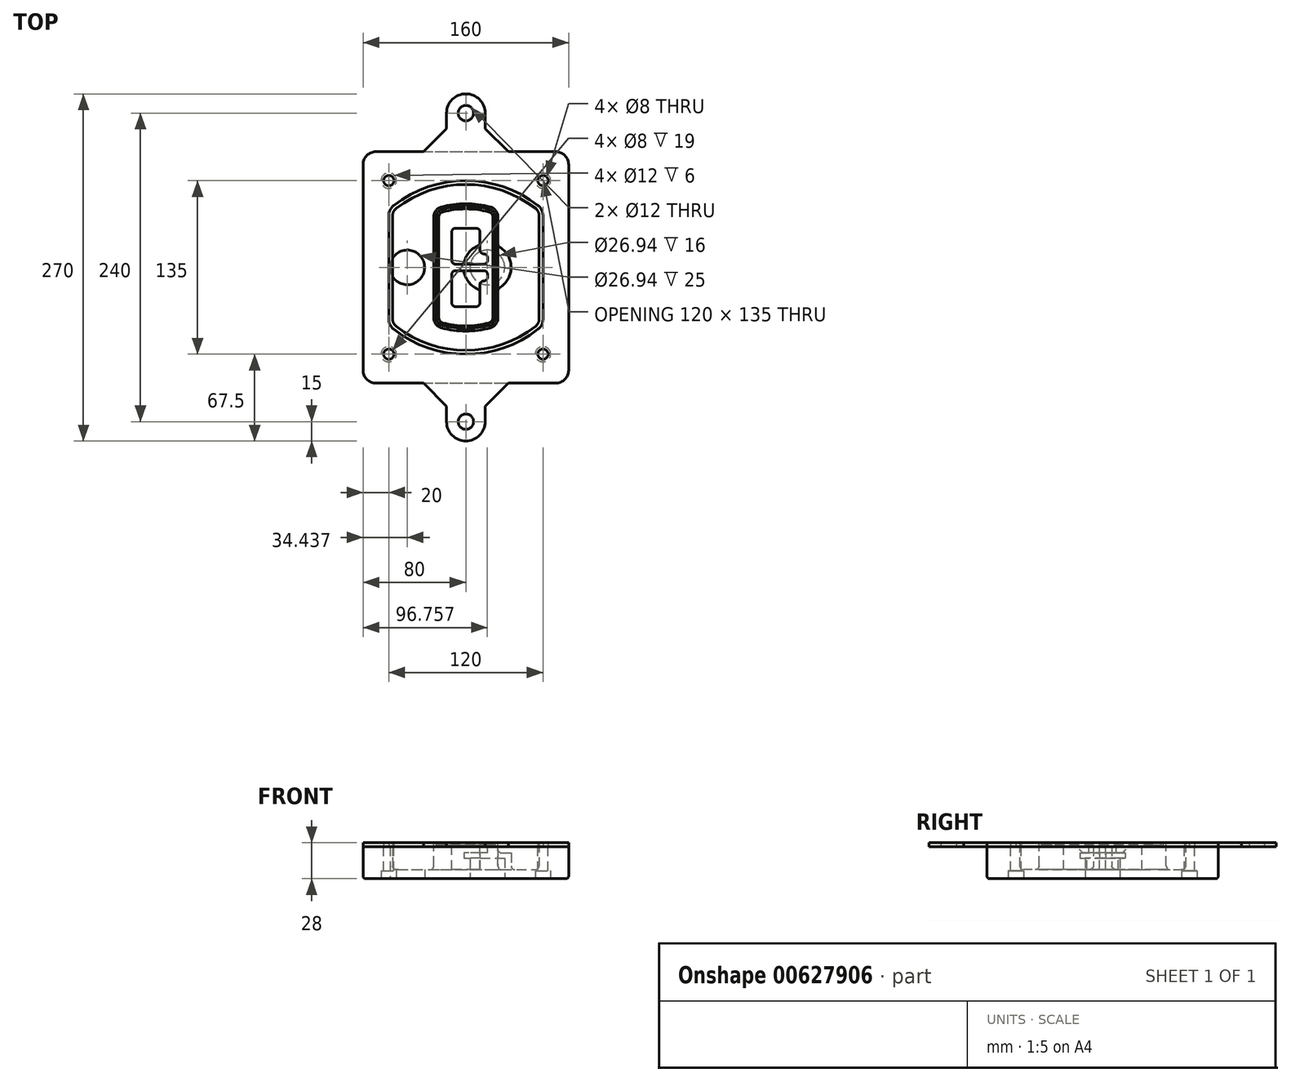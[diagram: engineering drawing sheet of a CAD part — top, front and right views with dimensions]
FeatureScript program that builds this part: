
annotation { "Feature Type Name" : "Feature", "Feature Type Description" : "" }
export const myFeature = defineFeature(function(context is Context, id is Id, definition is map)
    precondition{}
    {
        {
            var Q0;
            Q0=qCreatedBy(makeId("Top.planeOp"),FACE);
            var sketch = newSketch(context, id + "F0", { "sketchPlane" : qUnion([Q0])});
            skPoint(sketch, "E0.rect.middle", {"position": v(0, 0) * mm});
            skLineSegment(sketch, "E1.bottom", {"start": v(-70, -90) * mm, "end": v(70, -90) * mm});
            skLineSegment(sketch, "E1.top", {"start": v(-70, 90) * mm, "end": v(70, 90) * mm});
            skLineSegment(sketch, "E1.left", {"start": v(-80, -80) * mm, "end": v(-80, 80) * mm});
            skLineSegment(sketch, "E1.right", {"start": v(80, -80) * mm, "end": v(80, 80) * mm});
            skLineSegment(sketch, "E2", {"start": v(-80, 90) * mm, "end": v(80, -90) * mm, "construction": true});
            skLineSegment(sketch, "E3", {"start": v(80, 90) * mm, "end": v(-80, -90) * mm, "construction": true});
            skCircle(sketch, "E4", {"center": v(-60, 67.5) * mm, "radius": 4 * mm});
            skCircle(sketch, "E5", {"center": v(60, 67.5) * mm, "radius": 4 * mm});
            skCircle(sketch, "E6", {"center": v(60, -67.5) * mm, "radius": 4 * mm});
            skCircle(sketch, "E7", {"center": v(-60, -67.5) * mm, "radius": 4 * mm});
            skLineSegment(sketch, "E8", {"start": v(-60, 67.5) * mm, "end": v(60, 67.5) * mm, "construction": true});
            skLineSegment(sketch, "E9", {"start": v(60, 67.5) * mm, "end": v(60, -67.5) * mm, "construction": true});
            skLineSegment(sketch, "E10", {"start": v(60, -67.5) * mm, "end": v(-60, -67.5) * mm, "construction": true});
            skLineSegment(sketch, "E11", {"start": v(-60, -67.5) * mm, "end": v(-60, 67.5) * mm, "construction": true});
            skLineSegment(sketch, "E12", {"start": v(-60, 40.3) * mm, "end": v(-60, -40.3) * mm});
            skLineSegment(sketch, "E13", {"start": v(60, 40.3) * mm, "end": v(60, -40.3) * mm});
            skArc(sketch, "E14", {"start": v(56.15, 48.18) * mm, "mid": v(0, 67.5) * mm, "end": v(-56.15, 48.18) * mm});
            skArc(sketch, "E15", {"start": v(-56.15, -48.18) * mm, "mid": v(0, -67.5) * mm, "end": v(56.15, -48.18) * mm});
            skLineSegment(sketch, "E16", {"start": v(-60, 0) * mm, "end": v(60, 0) * mm, "construction": true});
            skPoint(sketch, "E17.visualSharp", {"position": v(-60, -45) * mm});
            skArc(sketch, "E17.filletArc", {"start": v(-60, -40.3) * mm, "mid": v(-58.99, -44.68) * mm, "end": v(-56.15, -48.18) * mm});
            skPoint(sketch, "E18.visualSharp", {"position": v(-60, 45) * mm});
            skArc(sketch, "E18.filletArc", {"start": v(-56.15, 48.18) * mm, "mid": v(-58.99, 44.68) * mm, "end": v(-60, 40.3) * mm});
            skPoint(sketch, "E19.visualSharp", {"position": v(60, 45) * mm});
            skArc(sketch, "E19.filletArc", {"start": v(60, 40.3) * mm, "mid": v(58.99, 44.68) * mm, "end": v(56.15, 48.18) * mm});
            skPoint(sketch, "E20.visualSharp", {"position": v(60, -45) * mm});
            skArc(sketch, "E20.filletArc", {"start": v(56.15, -48.18) * mm, "mid": v(58.99, -44.68) * mm, "end": v(60, -40.3) * mm});
            skPoint(sketch, "E21.visualSharp", {"position": v(-80, 90) * mm});
            skArc(sketch, "E21.filletArc", {"start": v(-70, 90) * mm, "mid": v(-77.07, 87.07) * mm, "end": v(-80, 80) * mm});
            skPoint(sketch, "E22.visualSharp", {"position": v(80, 90) * mm});
            skArc(sketch, "E22.filletArc", {"start": v(80, 80) * mm, "mid": v(77.07, 87.07) * mm, "end": v(70, 90) * mm});
            skPoint(sketch, "E23.visualSharp", {"position": v(80, -90) * mm});
            skArc(sketch, "E23.filletArc", {"start": v(70, -90) * mm, "mid": v(77.07, -87.07) * mm, "end": v(80, -80) * mm});
            skPoint(sketch, "E24.visualSharp", {"position": v(-80, -90) * mm});
            skArc(sketch, "E24.filletArc", {"start": v(-80, -80) * mm, "mid": v(-77.07, -87.07) * mm, "end": v(-70, -90) * mm});
            skArc(sketch, "E25.0", {"start": v(57, 40.3) * mm, "mid": v(56.3, 43.36) * mm, "end": v(54.3, 45.81) * mm});
            skLineSegment(sketch, "E25.1", {"start": v(57, 40.3) * mm, "end": v(57, -40.3) * mm});
            skArc(sketch, "E25.2", {"start": v(54.3, -45.81) * mm, "mid": v(56.3, -43.36) * mm, "end": v(57, -40.3) * mm});
            skArc(sketch, "E25.3", {"start": v(-54.3, -45.81) * mm, "mid": v(0, -64.5) * mm, "end": v(54.3, -45.81) * mm});
            skArc(sketch, "E25.4", {"start": v(-57, -40.3) * mm, "mid": v(-56.3, -43.36) * mm, "end": v(-54.3, -45.81) * mm});
            skArc(sketch, "E25.5", {"start": v(54.3, 45.81) * mm, "mid": v(0, 64.5) * mm, "end": v(-54.3, 45.81) * mm});
            skLineSegment(sketch, "E25.6", {"start": v(-57, 40.3) * mm, "end": v(-57, -40.3) * mm});
            skArc(sketch, "E25.7", {"start": v(-54.3, 45.81) * mm, "mid": v(-56.3, 43.36) * mm, "end": v(-57, 40.3) * mm});
            skArc(sketch, "E26.0", {"start": v(-58.62, 51.33) * mm, "mid": v(-62.58, 46.43) * mm, "end": v(-64, 40.3) * mm});
            skArc(sketch, "E26.1", {"start": v(58.62, 51.33) * mm, "mid": v(0, 71.5) * mm, "end": v(-58.62, 51.33) * mm});
            skArc(sketch, "E26.2", {"start": v(64, 40.3) * mm, "mid": v(62.58, 46.43) * mm, "end": v(58.62, 51.33) * mm});
            skLineSegment(sketch, "E26.3", {"start": v(64, 40.3) * mm, "end": v(64, -40.3) * mm});
            skArc(sketch, "E26.4", {"start": v(58.62, -51.33) * mm, "mid": v(62.58, -46.43) * mm, "end": v(64, -40.3) * mm});
            skLineSegment(sketch, "E26.5", {"start": v(-64, 40.3) * mm, "end": v(-64, -40.3) * mm});
            skArc(sketch, "E26.6", {"start": v(-58.62, -51.33) * mm, "mid": v(0, -71.5) * mm, "end": v(58.62, -51.33) * mm});
            skArc(sketch, "E26.7", {"start": v(-64, -40.3) * mm, "mid": v(-62.58, -46.43) * mm, "end": v(-58.62, -51.33) * mm});
            skSolve(sketch);
        }
        {
            var Q0;
            Q0=makeQuery(id+"F0.imprint","IMPRINT",FACE,{"disambiguationData":[TD([[makeQuery(id+"F0.imprint","IMPRINT",EDGE,{"derivedFrom":sQuery(id+"F0.wireOp",EDGE,"E1.bottom")}),1.0]])]});
            var Q1;
            Q1=makeQuery(id+"F0.imprint","IMPRINT",FACE,{"disambiguationData":[TD([[makeQuery(id+"F0.imprint","IMPRINT",EDGE,{"derivedFrom":sQuery(id+"F0.wireOp",EDGE,"E12")}),1.0]])]});
            var Q2;
            Q2=makeQuery(id+"F0.imprint","IMPRINT",FACE,{"disambiguationData":[TD([[makeQuery(id+"F0.imprint","IMPRINT",EDGE,{"derivedFrom":sQuery(id+"F0.wireOp",EDGE,"E25.0")}),1.0]])]});
            var Q3;
            Q3=makeQuery(id+"F0.imprint","IMPRINT",FACE,{"disambiguationData":[TD([[makeQuery(id+"F0.imprint","IMPRINT",EDGE,{"derivedFrom":sQuery(id+"F0.wireOp",EDGE,"E12")}),-1.0]])]});
            extrude(context, id + "F1", {"entities" : qUnion([Q0, Q1, Q2, Q3]), "oppositeDirection" : true, "depth" : 25 * mm});
        }
        {
            var Q0;
            Q0=makeQuery(id+"F0.imprint","IMPRINT",FACE,{"disambiguationData":[TD([[makeQuery(id+"F0.imprint","IMPRINT",EDGE,{"derivedFrom":sQuery(id+"F0.wireOp",EDGE,"E12")}),1.0]])]});
            extrude(context, id + "F2", {"entities" : qUnion([Q0]), "operationType" : NewBodyOperationType.ADD, "depth" : 3 * mm});
        }
        {
            var Q0;
            Q0=makeQuery(id+"F0.imprint","IMPRINT",FACE,{"disambiguationData":[TD([[makeQuery(id+"F0.imprint","IMPRINT",EDGE,{"derivedFrom":sQuery(id+"F0.wireOp",EDGE,"E25.0")}),1.0]])]});
            extrude(context, id + "F3", {"entities" : qUnion([Q0]), "operationType" : NewBodyOperationType.REMOVE, "oppositeDirection" : true, "depth" : 18 * mm});
        }
        {
            var Q0;
            Q0=makeQuery(id+"F2.opExtrude","CAP_FACE",FACE,{"disambiguationData":[OSD([sQuery(id+"F0.wireOp",EDGE,"E12"),sQuery(id+"F0.wireOp",EDGE,"E13"),sQuery(id+"F0.wireOp",EDGE,"E14"),sQuery(id+"F0.wireOp",EDGE,"E15"),sQuery(id+"F0.wireOp",EDGE,"E17.filletArc"),sQuery(id+"F0.wireOp",EDGE,"E18.filletArc"),sQuery(id+"F0.wireOp",EDGE,"E19.filletArc"),sQuery(id+"F0.wireOp",EDGE,"E20.filletArc"),sQuery(id+"F0.wireOp",EDGE,"E25.0"),sQuery(id+"F0.wireOp",EDGE,"E25.1"),sQuery(id+"F0.wireOp",EDGE,"E25.2"),sQuery(id+"F0.wireOp",EDGE,"E25.3"),sQuery(id+"F0.wireOp",EDGE,"E25.4"),sQuery(id+"F0.wireOp",EDGE,"E25.5"),sQuery(id+"F0.wireOp",EDGE,"E25.6"),sQuery(id+"F0.wireOp",EDGE,"E25.7")])],"isStart":false});
            var sketch = newSketch(context, id + "F4", { "sketchPlane" : qUnion([Q0])});
            skArc(sketch, "E27.0", {"start": v(-19.08, -46.97) * mm, "mid": v(0, -49.5) * mm, "end": v(19.08, -46.97) * mm});
            skArc(sketch, "E28.0", {"start": v(19.08, 46.97) * mm, "mid": v(0, 49.5) * mm, "end": v(-19.08, 46.97) * mm});
            skLineSegment(sketch, "E29", {"start": v(-25, 39.25) * mm, "end": v(-25, -39.25) * mm});
            skLineSegment(sketch, "E30", {"start": v(25, 39.25) * mm, "end": v(25, -39.25) * mm});
            skLineSegment(sketch, "E31", {"start": v(-25, 45.1) * mm, "end": v(25, 45.1) * mm, "construction": true});
            skLineSegment(sketch, "E32", {"start": v(-25, -45.1) * mm, "end": v(25, -45.1) * mm, "construction": true});
            skPoint(sketch, "E33.visualSharp", {"position": v(-25, 45.1) * mm});
            skArc(sketch, "E33.filletArc", {"start": v(-19.08, 46.97) * mm, "mid": v(-23.35, 44.11) * mm, "end": v(-25, 39.25) * mm});
            skPoint(sketch, "E34.visualSharp", {"position": v(25, 45.1) * mm});
            skArc(sketch, "E34.filletArc", {"start": v(25, 39.25) * mm, "mid": v(23.35, 44.11) * mm, "end": v(19.08, 46.97) * mm});
            skPoint(sketch, "E35.visualSharp", {"position": v(25, -45.1) * mm});
            skArc(sketch, "E35.filletArc", {"start": v(19.08, -46.97) * mm, "mid": v(23.35, -44.11) * mm, "end": v(25, -39.25) * mm});
            skPoint(sketch, "E36.visualSharp", {"position": v(-25, -45.1) * mm});
            skArc(sketch, "E36.filletArc", {"start": v(-25, -39.25) * mm, "mid": v(-23.35, -44.11) * mm, "end": v(-19.08, -46.97) * mm});
            skArc(sketch, "E37.0", {"start": v(54.3, 45.81) * mm, "mid": v(0, 64.5) * mm, "end": v(-54.3, 45.81) * mm});
            skArc(sketch, "E37.1", {"start": v(-54.3, 45.81) * mm, "mid": v(-56.3, 43.36) * mm, "end": v(-57, 40.3) * mm});
            skLineSegment(sketch, "E37.2", {"start": v(-57, 40.3) * mm, "end": v(-57, -40.3) * mm});
            skArc(sketch, "E37.3", {"start": v(-57, -40.3) * mm, "mid": v(-56.3, -43.36) * mm, "end": v(-54.3, -45.81) * mm});
            skArc(sketch, "E37.4", {"start": v(-54.3, -45.81) * mm, "mid": v(0, -64.5) * mm, "end": v(54.3, -45.81) * mm});
            skArc(sketch, "E37.5", {"start": v(54.3, -45.81) * mm, "mid": v(56.3, -43.36) * mm, "end": v(57, -40.3) * mm});
            skLineSegment(sketch, "E37.6", {"start": v(57, 40.3) * mm, "end": v(57, -40.3) * mm});
            skArc(sketch, "E37.7", {"start": v(57, 40.3) * mm, "mid": v(56.3, 43.36) * mm, "end": v(54.3, 45.81) * mm});
            skLineSegment(sketch, "E38.0", {"start": v(23, 39.25) * mm, "end": v(23, -39.25) * mm});
            skArc(sketch, "E38.1", {"start": v(18.56, -45.04) * mm, "mid": v(21.76, -42.9) * mm, "end": v(23, -39.25) * mm});
            skArc(sketch, "E38.2", {"start": v(-18.56, -45.04) * mm, "mid": v(0, -47.5) * mm, "end": v(18.56, -45.04) * mm});
            skArc(sketch, "E38.3", {"start": v(-23, -39.25) * mm, "mid": v(-21.76, -42.9) * mm, "end": v(-18.56, -45.04) * mm});
            skLineSegment(sketch, "E38.4", {"start": v(-23, 39.25) * mm, "end": v(-23, -39.25) * mm});
            skArc(sketch, "E38.5", {"start": v(23, 39.25) * mm, "mid": v(21.76, 42.9) * mm, "end": v(18.56, 45.04) * mm});
            skArc(sketch, "E38.6", {"start": v(-18.56, 45.04) * mm, "mid": v(-21.76, 42.9) * mm, "end": v(-23, 39.25) * mm});
            skArc(sketch, "E38.7", {"start": v(18.56, 45.04) * mm, "mid": v(0, 47.5) * mm, "end": v(-18.56, 45.04) * mm});
            skArc(sketch, "E39.0", {"start": v(21, 39.25) * mm, "mid": v(20.18, 41.68) * mm, "end": v(18.04, 43.1) * mm});
            skLineSegment(sketch, "E39.1", {"start": v(21, 39.25) * mm, "end": v(21, -39.25) * mm});
            skArc(sketch, "E39.2", {"start": v(18.04, -43.1) * mm, "mid": v(20.18, -41.68) * mm, "end": v(21, -39.25) * mm});
            skArc(sketch, "E39.3", {"start": v(-18.04, -43.1) * mm, "mid": v(0, -45.5) * mm, "end": v(18.04, -43.1) * mm});
            skArc(sketch, "E39.4", {"start": v(-21, -39.25) * mm, "mid": v(-20.18, -41.68) * mm, "end": v(-18.04, -43.1) * mm});
            skArc(sketch, "E39.5", {"start": v(18.04, 43.1) * mm, "mid": v(0, 45.5) * mm, "end": v(-18.04, 43.1) * mm});
            skLineSegment(sketch, "E39.6", {"start": v(-21, 39.25) * mm, "end": v(-21, -39.25) * mm});
            skArc(sketch, "E39.7", {"start": v(-18.04, 43.1) * mm, "mid": v(-20.18, 41.68) * mm, "end": v(-21, 39.25) * mm});
            skLineSegment(sketch, "E40", {"start": v(-25, 0) * mm, "end": v(25, 0) * mm, "construction": true});
            skLineSegment(sketch, "E41", {"start": v(-11, 5.5) * mm, "end": v(-11, 27.5) * mm});
            skLineSegment(sketch, "E42", {"start": v(-8, 30.5) * mm, "end": v(8, 30.5) * mm});
            skLineSegment(sketch, "E43", {"start": v(11, 27.5) * mm, "end": v(11, 13.5) * mm});
            skLineSegment(sketch, "E44", {"start": v(14, 10.5) * mm, "end": v(14, 10.5) * mm});
            skLineSegment(sketch, "E45", {"start": v(17, 7.5) * mm, "end": v(17, 5.5) * mm});
            skLineSegment(sketch, "E46", {"start": v(14, 2.5) * mm, "end": v(-8, 2.5) * mm});
            skPoint(sketch, "E47.visualSharp", {"position": v(-11, 30.5) * mm});
            skArc(sketch, "E47.filletArc", {"start": v(-8, 30.5) * mm, "mid": v(-10.12, 29.62) * mm, "end": v(-11, 27.5) * mm});
            skPoint(sketch, "E48.visualSharp", {"position": v(11, 30.5) * mm});
            skArc(sketch, "E48.filletArc", {"start": v(11, 27.5) * mm, "mid": v(10.12, 29.62) * mm, "end": v(8, 30.5) * mm});
            skPoint(sketch, "E49.visualSharp", {"position": v(11, 10.5) * mm});
            skArc(sketch, "E49.filletArc", {"start": v(11, 13.5) * mm, "mid": v(11.88, 11.38) * mm, "end": v(14, 10.5) * mm});
            skPoint(sketch, "E50.visualSharp", {"position": v(17, 10.5) * mm});
            skArc(sketch, "E50.filletArc", {"start": v(17, 7.5) * mm, "mid": v(16.12, 9.62) * mm, "end": v(14, 10.5) * mm});
            skPoint(sketch, "E51.visualSharp", {"position": v(17, 2.5) * mm});
            skArc(sketch, "E51.filletArc", {"start": v(14, 2.5) * mm, "mid": v(16.12, 3.38) * mm, "end": v(17, 5.5) * mm});
            skPoint(sketch, "E52.visualSharp", {"position": v(-11, 2.5) * mm});
            skArc(sketch, "E52.filletArc", {"start": v(-11, 5.5) * mm, "mid": v(-10.12, 3.38) * mm, "end": v(-8, 2.5) * mm});
            skLineSegment(sketch, "E53.0.MirrorCS", {"start": v(14, -2.5) * mm, "end": v(-8, -2.5) * mm});
            skArc(sketch, "E54.0.MirrorCS", {"start": v(-11, -5.5) * mm, "mid": v(-10.12, -3.38) * mm, "end": v(-8, -2.5) * mm});
            skLineSegment(sketch, "E55.0.MirrorCS", {"start": v(-11, -5.5) * mm, "end": v(-11, -27.5) * mm});
            skArc(sketch, "E56.0.MirrorCS", {"start": v(-8, -30.5) * mm, "mid": v(-10.12, -29.62) * mm, "end": v(-11, -27.5) * mm});
            skLineSegment(sketch, "E57.0.MirrorCS", {"start": v(-8, -30.5) * mm, "end": v(8, -30.5) * mm});
            skArc(sketch, "E58.0.MirrorCS", {"start": v(11, -27.5) * mm, "mid": v(10.12, -29.62) * mm, "end": v(8, -30.5) * mm});
            skLineSegment(sketch, "E59.0.MirrorCS", {"start": v(11, -27.5) * mm, "end": v(11, -13.5) * mm});
            skArc(sketch, "E60.0.MirrorCS", {"start": v(11, -13.5) * mm, "mid": v(11.88, -11.38) * mm, "end": v(14, -10.5) * mm});
            skArc(sketch, "E61.0.MirrorCS", {"start": v(17, -7.5) * mm, "mid": v(16.12, -9.62) * mm, "end": v(14, -10.5) * mm});
            skLineSegment(sketch, "E62.0.MirrorCS", {"start": v(17, -7.5) * mm, "end": v(17, -5.5) * mm});
            skArc(sketch, "E63.0.MirrorCS", {"start": v(14, -2.5) * mm, "mid": v(16.12, -3.38) * mm, "end": v(17, -5.5) * mm});
            skSolve(sketch);
        }
        {
            var Q0;
            Q0=makeQuery(id+"F4.imprint","IMPRINT",FACE,{"disambiguationData":[TD([[makeQuery(id+"F4.imprint","IMPRINT",EDGE,{"derivedFrom":sQuery(id+"F4.wireOp",EDGE,"E27.0")}),1.0]])]});
            var Q1;
            Q1=makeQuery(id+"F4.imprint","IMPRINT",FACE,{"disambiguationData":[TD([[makeQuery(id+"F4.imprint","IMPRINT",EDGE,{"derivedFrom":sQuery(id+"F4.wireOp",EDGE,"E38.0")}),-1.0]])]});
            var Q2;
            Q2=makeQuery(id+"F4.imprint","IMPRINT",FACE,{"disambiguationData":[TD([[makeQuery(id+"F4.imprint","IMPRINT",EDGE,{"derivedFrom":sQuery(id+"F4.wireOp",EDGE,"E39.0")}),1.0]])]});
            extrude(context, id + "F5", {"entities" : qUnion([Q0, Q1, Q2]), "operationType" : NewBodyOperationType.ADD, "endBound" : BoundingType.UP_TO_NEXT, "oppositeDirection" : true, "depth" : 25 * mm});
        }
        {
            var Q0;
            Q0=makeQuery(id+"F4.imprint","IMPRINT",FACE,{"disambiguationData":[TD([[makeQuery(id+"F4.imprint","IMPRINT",EDGE,{"derivedFrom":sQuery(id+"F4.wireOp",EDGE,"E38.0")}),-1.0]])]});
            extrude(context, id + "F6", {"entities" : qUnion([Q0]), "operationType" : NewBodyOperationType.REMOVE, "oppositeDirection" : true, "depth" : 2 * mm});
        }
        {
            var Q0;
            Q0=makeQuery(id+"F1.opExtrude","CAP_FACE",FACE,{"disambiguationData":[OSD([sQuery(id+"F0.wireOp",EDGE,"E1.bottom"),sQuery(id+"F0.wireOp",EDGE,"E1.top"),sQuery(id+"F0.wireOp",EDGE,"E1.left"),sQuery(id+"F0.wireOp",EDGE,"E1.right"),sQuery(id+"F0.wireOp",EDGE,"E4"),sQuery(id+"F0.wireOp",EDGE,"E5"),sQuery(id+"F0.wireOp",EDGE,"E6"),sQuery(id+"F0.wireOp",EDGE,"E7"),sQuery(id+"F0.wireOp",EDGE,"E21.filletArc"),sQuery(id+"F0.wireOp",EDGE,"E22.filletArc"),sQuery(id+"F0.wireOp",EDGE,"E23.filletArc"),sQuery(id+"F0.wireOp",EDGE,"E24.filletArc")])],"isStart":false});
            var sketch = newSketch(context, id + "F7", { "sketchPlane" : qUnion([Q0])});
            skCircle(sketch, "E64", {"center": v(16.76, 0) * mm, "radius": 13.47 * mm});
            skCircle(sketch, "E65", {"center": v(-45.56, 0) * mm, "radius": 13.47 * mm});
            skLineSegment(sketch, "E66", {"start": v(80, 0) * mm, "end": v(-80, 0) * mm});
            skCircle(sketch, "E67", {"center": v(16.76, 0) * mm, "radius": 18.47 * mm});
            skCircle(sketch, "E68", {"center": v(60, -67.5) * mm, "radius": 6 * mm});
            skCircle(sketch, "E69", {"center": v(-60, -67.5) * mm, "radius": 6 * mm});
            skCircle(sketch, "E70", {"center": v(-60, 67.5) * mm, "radius": 6 * mm});
            skCircle(sketch, "E71", {"center": v(60, 67.5) * mm, "radius": 6 * mm});
            skSolve(sketch);
        }
        {
            var Q0;
            {var subQ1=sQuery(id+"F7.wireOp",EDGE,"E66");var subQ4=sQuery(id+"F7.wireOp",EDGE,"E64");var subQ6=makeQuery(id+"F7.imprint","INTERSECT",VERTEX,{"disambiguationData":[OD(0.0)],"derivedFrom":[subQ4,subQ1]});Q0=makeQuery(id+"F7.imprint","IMPRINT",FACE,{"disambiguationData":[TD([[makeQuery(id+"F7.imprint","IMPRINT",EDGE,{"disambiguationData":[TD([[subQ6,-1.0]])],"derivedFrom":subQ4}),-1.0]])]});}
            var Q1;
            {var subQ0=sQuery(id+"F7.wireOp",EDGE,"E66");var subQ1=sQuery(id+"F7.wireOp",EDGE,"E64");var subQ3=makeQuery(id+"F7.imprint","INTERSECT",VERTEX,{"disambiguationData":[OD(0.0)],"derivedFrom":[subQ1,subQ0]});Q1=makeQuery(id+"F7.imprint","IMPRINT",FACE,{"disambiguationData":[TD([[makeQuery(id+"F7.imprint","IMPRINT",EDGE,{"disambiguationData":[TD([[subQ3,-1.0]])],"derivedFrom":subQ1}),1.0]])]});}
            var Q2;
            {var subQ0=sQuery(id+"F7.wireOp",EDGE,"E66");var subQ1=sQuery(id+"F7.wireOp",EDGE,"E64");var subQ3=makeQuery(id+"F7.imprint","INTERSECT",VERTEX,{"disambiguationData":[OD(0.0)],"derivedFrom":[subQ1,subQ0]});Q2=makeQuery(id+"F7.imprint","IMPRINT",FACE,{"disambiguationData":[TD([[makeQuery(id+"F7.imprint","IMPRINT",EDGE,{"disambiguationData":[TD([[subQ3,1.0]])],"derivedFrom":subQ1}),1.0]])]});}
            var Q3;
            {var subQ1=sQuery(id+"F7.wireOp",EDGE,"E66");var subQ4=sQuery(id+"F7.wireOp",EDGE,"E64");var subQ6=makeQuery(id+"F7.imprint","INTERSECT",VERTEX,{"disambiguationData":[OD(0.0)],"derivedFrom":[subQ4,subQ1]});Q3=makeQuery(id+"F7.imprint","IMPRINT",FACE,{"disambiguationData":[TD([[makeQuery(id+"F7.imprint","IMPRINT",EDGE,{"disambiguationData":[TD([[subQ6,1.0]])],"derivedFrom":subQ4}),-1.0]])]});}
            extrude(context, id + "F8", {"entities" : qUnion([Q0, Q1, Q2, Q3]), "operationType" : NewBodyOperationType.ADD, "oppositeDirection" : true, "depth" : 20 * mm});
        }
        {
            var Q0;
            {var subQ0=sQuery(id+"F7.wireOp",EDGE,"E66");var subQ1=sQuery(id+"F7.wireOp",EDGE,"E64");var subQ3=makeQuery(id+"F7.imprint","INTERSECT",VERTEX,{"disambiguationData":[OD(0.0)],"derivedFrom":[subQ1,subQ0]});Q0=makeQuery(id+"F7.imprint","IMPRINT",FACE,{"disambiguationData":[TD([[makeQuery(id+"F7.imprint","IMPRINT",EDGE,{"disambiguationData":[TD([[subQ3,-1.0]])],"derivedFrom":subQ1}),1.0]])]});}
            var Q1;
            {var subQ0=sQuery(id+"F7.wireOp",EDGE,"E66");var subQ1=sQuery(id+"F7.wireOp",EDGE,"E64");var subQ3=makeQuery(id+"F7.imprint","INTERSECT",VERTEX,{"disambiguationData":[OD(0.0)],"derivedFrom":[subQ1,subQ0]});Q1=makeQuery(id+"F7.imprint","IMPRINT",FACE,{"disambiguationData":[TD([[makeQuery(id+"F7.imprint","IMPRINT",EDGE,{"disambiguationData":[TD([[subQ3,1.0]])],"derivedFrom":subQ1}),1.0]])]});}
            extrude(context, id + "F9", {"entities" : qUnion([Q0, Q1]), "operationType" : NewBodyOperationType.REMOVE, "oppositeDirection" : true, "depth" : 16 * mm});
        }
        {
            var Q0;
            {var subQ0=sQuery(id+"F7.wireOp",EDGE,"E66");var subQ1=sQuery(id+"F7.wireOp",EDGE,"E65");var subQ3=makeQuery(id+"F7.imprint","INTERSECT",VERTEX,{"disambiguationData":[OD(0.0)],"derivedFrom":[subQ1,subQ0]});Q0=makeQuery(id+"F7.imprint","IMPRINT",FACE,{"disambiguationData":[TD([[makeQuery(id+"F7.imprint","IMPRINT",EDGE,{"disambiguationData":[TD([[subQ3,-1.0]])],"derivedFrom":subQ1}),1.0]])]});}
            var Q1;
            {var subQ0=sQuery(id+"F7.wireOp",EDGE,"E66");var subQ1=sQuery(id+"F7.wireOp",EDGE,"E65");var subQ3=makeQuery(id+"F7.imprint","INTERSECT",VERTEX,{"disambiguationData":[OD(0.0)],"derivedFrom":[subQ1,subQ0]});Q1=makeQuery(id+"F7.imprint","IMPRINT",FACE,{"disambiguationData":[TD([[makeQuery(id+"F7.imprint","IMPRINT",EDGE,{"disambiguationData":[TD([[subQ3,1.0]])],"derivedFrom":subQ1}),1.0]])]});}
            extrude(context, id + "F10", {"entities" : qUnion([Q0, Q1]), "operationType" : NewBodyOperationType.REMOVE, "oppositeDirection" : true, "depth" : 25 * mm});
        }
        {
            var Q0;
            Q0=makeQuery(id+"F7.imprint","IMPRINT",FACE,{"disambiguationData":[TD([[makeQuery(id+"F7.imprint","IMPRINT",EDGE,{"derivedFrom":sQuery(id+"F7.wireOp",EDGE,"E68")}),1.0]])]});
            var Q1;
            Q1=makeQuery(id+"F7.imprint","IMPRINT",FACE,{"disambiguationData":[TD([[makeQuery(id+"F7.imprint","IMPRINT",EDGE,{"derivedFrom":makeQuery(id+"F1.opExtrude","CAP_EDGE",EDGE,{"disambiguationData":[OSD([sQuery(id+"F0.wireOp",EDGE,"E5")])],"isStart":false})}),-1.0]])]});
            var Q2;
            Q2=makeQuery(id+"F7.imprint","IMPRINT",FACE,{"disambiguationData":[TD([[makeQuery(id+"F7.imprint","IMPRINT",EDGE,{"derivedFrom":sQuery(id+"F7.wireOp",EDGE,"E69")}),1.0]])]});
            var Q3;
            Q3=makeQuery(id+"F7.imprint","IMPRINT",FACE,{"disambiguationData":[TD([[makeQuery(id+"F7.imprint","IMPRINT",EDGE,{"derivedFrom":makeQuery(id+"F1.opExtrude","CAP_EDGE",EDGE,{"disambiguationData":[OSD([sQuery(id+"F0.wireOp",EDGE,"E4")])],"isStart":false})}),-1.0]])]});
            var Q4;
            Q4=makeQuery(id+"F7.imprint","IMPRINT",FACE,{"disambiguationData":[TD([[makeQuery(id+"F7.imprint","IMPRINT",EDGE,{"derivedFrom":sQuery(id+"F7.wireOp",EDGE,"E70")}),1.0]])]});
            var Q5;
            Q5=makeQuery(id+"F7.imprint","IMPRINT",FACE,{"disambiguationData":[TD([[makeQuery(id+"F7.imprint","IMPRINT",EDGE,{"derivedFrom":makeQuery(id+"F1.opExtrude","CAP_EDGE",EDGE,{"disambiguationData":[OSD([sQuery(id+"F0.wireOp",EDGE,"E7")])],"isStart":false})}),-1.0]])]});
            var Q6;
            Q6=makeQuery(id+"F7.imprint","IMPRINT",FACE,{"disambiguationData":[TD([[makeQuery(id+"F7.imprint","IMPRINT",EDGE,{"derivedFrom":sQuery(id+"F7.wireOp",EDGE,"E71")}),1.0]])]});
            var Q7;
            Q7=makeQuery(id+"F7.imprint","IMPRINT",FACE,{"disambiguationData":[TD([[makeQuery(id+"F7.imprint","IMPRINT",EDGE,{"derivedFrom":makeQuery(id+"F1.opExtrude","CAP_EDGE",EDGE,{"disambiguationData":[OSD([sQuery(id+"F0.wireOp",EDGE,"E6")])],"isStart":false})}),-1.0]])]});
            extrude(context, id + "F11", {"entities" : qUnion([Q0, Q1, Q2, Q3, Q4, Q5, Q6, Q7]), "operationType" : NewBodyOperationType.REMOVE, "oppositeDirection" : true, "depth" : 6 * mm});
        }
        {
            var Q0;
            Q0=makeQuery(id+"F9.boolean.opBoolean","COPY",FACE,{"derivedFrom":makeQuery(id+"F9.opExtrude","CAP_FACE",FACE,{"disambiguationData":[OSD([sQuery(id+"F7.wireOp",EDGE,"E64")])],"isStart":false})});
            var sketch = newSketch(context, id + "F12", { "sketchPlane" : qUnion([Q0])});
            skArc(sketch, "E72.0", {"start": v(11, 17.55) * mm, "mid": v(2.57, 11.82) * mm, "end": v(-1.54, 2.5) * mm});
            skArc(sketch, "E72.1", {"start": v(-1.54, -2.5) * mm, "mid": v(2.57, -11.82) * mm, "end": v(11, -17.55) * mm});
            skLineSegment(sketch, "E73", {"start": v(-1.54, -2.5) * mm, "end": v(14, -2.5) * mm});
            skLineSegment(sketch, "E74.0", {"start": v(14, 2.5) * mm, "end": v(-1.54, 2.5) * mm});
            skArc(sketch, "E74.1", {"start": v(14, 2.5) * mm, "mid": v(16.12, 3.38) * mm, "end": v(17, 5.5) * mm});
            skLineSegment(sketch, "E74.2", {"start": v(17, 7.5) * mm, "end": v(17, 5.5) * mm});
            skArc(sketch, "E74.3", {"start": v(17, 7.5) * mm, "mid": v(16.12, 9.62) * mm, "end": v(14, 10.5) * mm});
            skArc(sketch, "E74.4", {"start": v(11, 13.5) * mm, "mid": v(11.88, 11.38) * mm, "end": v(14, 10.5) * mm});
            skLineSegment(sketch, "E74.5", {"start": v(11, 17.55) * mm, "end": v(11, 13.5) * mm});
            skLineSegment(sketch, "E74.7", {"start": v(14, -2.5) * mm, "end": v(-1.54, -2.5) * mm});
            skArc(sketch, "E74.8", {"start": v(14, -2.5) * mm, "mid": v(16.12, -3.38) * mm, "end": v(17, -5.5) * mm});
            skLineSegment(sketch, "E74.9", {"start": v(17, -7.5) * mm, "end": v(17, -5.5) * mm});
            skArc(sketch, "E74.10", {"start": v(17, -7.5) * mm, "mid": v(16.12, -9.62) * mm, "end": v(14, -10.5) * mm});
            skArc(sketch, "E74.11", {"start": v(11, -13.5) * mm, "mid": v(11.88, -11.38) * mm, "end": v(14, -10.5) * mm});
            skLineSegment(sketch, "E74.12", {"start": v(11, -17.55) * mm, "end": v(11, -13.5) * mm});
            skPoint(sketch, "E75.orphan", {"position": v(11, -27.5) * mm});
            skPoint(sketch, "E76.orphan", {"position": v(-8, -2.5) * mm});
            skPoint(sketch, "E77.orphan", {"position": v(-8, 2.5) * mm});
            skPoint(sketch, "E78.orphan", {"position": v(11, 27.5) * mm});
            skSolve(sketch);
        }
        {
            var Q0;
            {var subQ7=sQuery(id+"F12.wireOp",EDGE,"E72.0");var subQ14=sQuery(id+"F12.wireOp",EDGE,"E72.1");var subQ16=sQuery(id+"F12.wireOp",EDGE,"E74.1");var subQ18=sQuery(id+"F12.wireOp",EDGE,"E74.8");Q0=qUnion([makeQuery(id+"F12.imprint","IMPRINT",FACE,{"disambiguationData":[TD([[makeQuery(id+"F12.imprint","IMPRINT",EDGE,{"derivedFrom":subQ7}),1.0]])]}),makeQuery(id+"F12.imprint","IMPRINT",FACE,{"disambiguationData":[TD([[makeQuery(id+"F12.imprint","IMPRINT",EDGE,{"derivedFrom":subQ14}),1.0]])]}),makeQuery(id+"F12.imprint","IMPRINT",FACE,{"disambiguationData":[TD([[makeQuery(id+"F12.imprint","IMPRINT",EDGE,{"derivedFrom":subQ16}),1.0]])]}),makeQuery(id+"F12.imprint","IMPRINT",FACE,{"disambiguationData":[TD([[makeQuery(id+"F12.imprint","IMPRINT",EDGE,{"derivedFrom":subQ18}),-1.0]])]})]);}
            var Q1;
            Q1=makeQuery(id+"F5.boolean.opBoolean","SPLIT",FACE,{"disambiguationData":[TD([makeQuery(id+"F5.opExtrude","SWEPT_FACE",FACE,{"disambiguationData":[OSD([sQuery(id+"F4.wireOp",EDGE,"E41")])]})])],"derivedFrom":makeQuery(id+"F3.boolean.opBoolean","COPY",FACE,{"derivedFrom":makeQuery(id+"F3.opExtrude","CAP_FACE",FACE,{"disambiguationData":[OSD([sQuery(id+"F0.wireOp",EDGE,"E25.0"),sQuery(id+"F0.wireOp",EDGE,"E25.1"),sQuery(id+"F0.wireOp",EDGE,"E25.2"),sQuery(id+"F0.wireOp",EDGE,"E25.3"),sQuery(id+"F0.wireOp",EDGE,"E25.4"),sQuery(id+"F0.wireOp",EDGE,"E25.5"),sQuery(id+"F0.wireOp",EDGE,"E25.6"),sQuery(id+"F0.wireOp",EDGE,"E25.7")])],"isStart":false})})});
            extrude(context, id + "F13", {"entities" : qUnion([Q0]), "operationType" : NewBodyOperationType.REMOVE, "endBound" : BoundingType.UP_TO_SURFACE, "endBoundEntityFace" : qUnion([Q1]), "depth" : 25 * mm});
        }
        {
            var Q0;
            Q0=makeQuery(id+"F3.boolean.opBoolean","COPY",EDGE,{"derivedFrom":makeQuery(id+"F3.opExtrude","CAP_EDGE",EDGE,{"disambiguationData":[OSD([sQuery(id+"F0.wireOp",EDGE,"E25.6")])],"isStart":false})});
            var Q1;
            Q1=makeQuery(id+"F8.boolean.opBoolean","INTERSECT",EDGE,{"derivedFrom":[makeQuery(id+"F5.opExtrude","SWEPT_FACE",FACE,{"disambiguationData":[OSD([sQuery(id+"F4.wireOp",EDGE,"E30")])]}),makeQuery(id+"F8.opExtrude","CAP_FACE",FACE,{"disambiguationData":[OSD([sQuery(id+"F7.wireOp",EDGE,"E67")])],"isStart":false})]});
            var Q2;
            Q2=makeQuery(id+"F8.boolean.opBoolean","INTERSECT",EDGE,{"disambiguationData":[OD(1.0)],"derivedFrom":[makeQuery(id+"F5.opExtrude","SWEPT_FACE",FACE,{"disambiguationData":[OSD([sQuery(id+"F4.wireOp",EDGE,"E30")])]}),makeQuery(id+"F8.opExtrude","SWEPT_FACE",FACE,{"disambiguationData":[OSD([sQuery(id+"F7.wireOp",EDGE,"E67")])]})]});
            var Q3;
            {var subQ0=sQuery(id+"F4.wireOp",EDGE,"E30");Q3=makeQuery(id+"F8.boolean.opBoolean","SPLIT",EDGE,{"disambiguationData":[TD([makeQuery(id+"F5.opExtrude","SWEPT_FACE",FACE,{"disambiguationData":[OSD([sQuery(id+"F4.wireOp",EDGE,"E35.filletArc")])]})])],"derivedFrom":makeQuery(id+"F5.opExtrude","CAP_EDGE",EDGE,{"disambiguationData":[OSD([subQ0])],"isStart":false})});}
            var Q4;
            {var subQ0=sQuery(id+"F0.wireOp",EDGE,"E25.7");var subQ1=sQuery(id+"F0.wireOp",EDGE,"E25.1");var subQ2=sQuery(id+"F0.wireOp",EDGE,"E25.6");var subQ3=sQuery(id+"F0.wireOp",EDGE,"E25.5");var subQ4=sQuery(id+"F0.wireOp",EDGE,"E25.4");var subQ5=sQuery(id+"F0.wireOp",EDGE,"E25.0");var subQ6=sQuery(id+"F0.wireOp",EDGE,"E25.2");var subQ7=sQuery(id+"F0.wireOp",EDGE,"E25.3");Q4=makeQuery(id+"F8.boolean.opBoolean","INTERSECT",EDGE,{"derivedFrom":[makeQuery(id+"F5.boolean.opBoolean","SPLIT",FACE,{"disambiguationData":[TD([makeQuery(id+"F2.opExtrude","SWEPT_FACE",FACE,{"disambiguationData":[OSD([subQ5])]})])],"derivedFrom":makeQuery(id+"F3.boolean.opBoolean","COPY",FACE,{"derivedFrom":makeQuery(id+"F3.opExtrude","CAP_FACE",FACE,{"disambiguationData":[OSD([subQ5,subQ1,subQ6,subQ7,subQ4,subQ3,subQ2,subQ0])],"isStart":false})})}),makeQuery(id+"F8.opExtrude","SWEPT_FACE",FACE,{"disambiguationData":[OSD([sQuery(id+"F7.wireOp",EDGE,"E67")])]})]});}
            var Q5;
            Q5=makeQuery(id+"F8.boolean.opBoolean","INTERSECT",EDGE,{"disambiguationData":[OD(0.0)],"derivedFrom":[makeQuery(id+"F5.opExtrude","SWEPT_FACE",FACE,{"disambiguationData":[OSD([sQuery(id+"F4.wireOp",EDGE,"E30")])]}),makeQuery(id+"F8.opExtrude","SWEPT_FACE",FACE,{"disambiguationData":[OSD([sQuery(id+"F7.wireOp",EDGE,"E67")])]})]});
            fillet(context, id + "F14", {"entities" : qUnion([Q0, Q1, Q2, Q3, Q4, Q5]), "radius" : 3 * mm, "tangentPropagation" : true, "allowEdgeOverflow" : false});
        }
        {
            var Q0;
            Q0=makeQuery(id+"F1.opExtrude","CAP_EDGE",EDGE,{"disambiguationData":[OSD([sQuery(id+"F0.wireOp",EDGE,"E1.bottom")])],"isStart":false});
            fillet(context, id + "F15", {"entities" : qUnion([Q0]), "radius" : 2 * mm, "tangentPropagation" : true, "allowEdgeOverflow" : false});
        }
        {
            var Q0;
            {var subQ0=sQuery(id+"F0.wireOp",EDGE,"E21.filletArc");var subQ1=sQuery(id+"F0.wireOp",EDGE,"E7");var subQ2=sQuery(id+"F0.wireOp",EDGE,"E6");var subQ3=sQuery(id+"F0.wireOp",EDGE,"E5");var subQ4=sQuery(id+"F0.wireOp",EDGE,"E4");var subQ5=sQuery(id+"F0.wireOp",EDGE,"E22.filletArc");var subQ6=sQuery(id+"F0.wireOp",EDGE,"E1.bottom");var subQ7=sQuery(id+"F0.wireOp",EDGE,"E1.right");var subQ8=sQuery(id+"F0.wireOp",EDGE,"E1.top");var subQ9=sQuery(id+"F0.wireOp",EDGE,"E1.left");var subQ10=sQuery(id+"F0.wireOp",EDGE,"E23.filletArc");var subQ11=sQuery(id+"F0.wireOp",EDGE,"E24.filletArc");Q0=makeQuery(id+"F2.boolean.opBoolean","SPLIT",FACE,{"disambiguationData":[TD([makeQuery(id+"F1.opExtrude","SWEPT_FACE",FACE,{"disambiguationData":[OSD([subQ6])]})])],"derivedFrom":makeQuery(id+"F1.opExtrude","CAP_FACE",FACE,{"disambiguationData":[OSD([subQ6,subQ8,subQ9,subQ7,subQ4,subQ3,subQ2,subQ1,subQ0,subQ5,subQ10,subQ11])],"isStart":true})});}
            var sketch = newSketch(context, id + "F16", { "sketchPlane" : qUnion([Q0])});
            skLineSegment(sketch, "E79.0", {"start": v(-70, 90) * mm, "end": v(70, 90) * mm});
            skArc(sketch, "E79.1", {"start": v(-70, 90) * mm, "mid": v(-77.07, 87.07) * mm, "end": v(-80, 80) * mm});
            skLineSegment(sketch, "E79.2", {"start": v(-80, -80) * mm, "end": v(-80, 80) * mm});
            skArc(sketch, "E79.3", {"start": v(-80, -80) * mm, "mid": v(-77.07, -87.07) * mm, "end": v(-70, -90) * mm});
            skLineSegment(sketch, "E79.4", {"start": v(-70, -90) * mm, "end": v(70, -90) * mm});
            skLineSegment(sketch, "E79.5", {"start": v(80, -80) * mm, "end": v(80, 80) * mm});
            skArc(sketch, "E79.6", {"start": v(70, -90) * mm, "mid": v(77.07, -87.07) * mm, "end": v(80, -80) * mm});
            skArc(sketch, "E79.7", {"start": v(80, 80) * mm, "mid": v(77.07, 87.07) * mm, "end": v(70, 90) * mm});
            skArc(sketch, "E79.8", {"start": v(56.15, 48.18) * mm, "mid": v(0, 67.5) * mm, "end": v(-56.15, 48.18) * mm});
            skArc(sketch, "E79.9", {"start": v(60, 40.3) * mm, "mid": v(58.99, 44.68) * mm, "end": v(56.15, 48.18) * mm});
            skLineSegment(sketch, "E79.10", {"start": v(60, 40.3) * mm, "end": v(60, -40.3) * mm});
            skArc(sketch, "E79.11", {"start": v(56.15, -48.18) * mm, "mid": v(58.99, -44.68) * mm, "end": v(60, -40.3) * mm});
            skArc(sketch, "E79.12", {"start": v(-56.15, -48.18) * mm, "mid": v(0, -67.5) * mm, "end": v(56.15, -48.18) * mm});
            skArc(sketch, "E79.13", {"start": v(-60, -40.3) * mm, "mid": v(-58.99, -44.68) * mm, "end": v(-56.15, -48.18) * mm});
            skLineSegment(sketch, "E79.14", {"start": v(-60, 40.3) * mm, "end": v(-60, -40.3) * mm});
            skArc(sketch, "E79.15", {"start": v(-56.15, 48.18) * mm, "mid": v(-58.99, 44.68) * mm, "end": v(-60, 40.3) * mm});
            skLineSegment(sketch, "E80", {"start": v(0, 90) * mm, "end": v(0, 120) * mm, "construction": true});
            skCircle(sketch, "E81", {"center": v(0, 120) * mm, "radius": 6 * mm});
            skArc(sketch, "E82", {"start": v(15, 120) * mm, "mid": v(0, 135) * mm, "end": v(-15, 120) * mm});
            skLineSegment(sketch, "E83", {"start": v(-15, 120) * mm, "end": v(-15, 108) * mm});
            skLineSegment(sketch, "E84", {"start": v(-15, 108) * mm, "end": v(-33, 90) * mm});
            skLineSegment(sketch, "E85", {"start": v(15, 120) * mm, "end": v(15, 108) * mm});
            skLineSegment(sketch, "E86", {"start": v(15, 108) * mm, "end": v(33, 90) * mm});
            skLineSegment(sketch, "E87", {"start": v(-80, 0) * mm, "end": v(80, 0) * mm, "construction": true});
            skCircle(sketch, "E88.MirrorC", {"center": v(0, -120) * mm, "radius": 6 * mm});
            skLineSegment(sketch, "E89.MirrorCS", {"start": v(0, -90) * mm, "end": v(0, -120) * mm, "construction": true});
            skLineSegment(sketch, "E90.MirrorCS", {"start": v(-15, -120) * mm, "end": v(-15, -108) * mm});
            skLineSegment(sketch, "E91.MirrorCS", {"start": v(-15, -108) * mm, "end": v(-33, -90) * mm});
            skLineSegment(sketch, "E92.MirrorCS", {"start": v(15, -108) * mm, "end": v(33, -90) * mm});
            skLineSegment(sketch, "E93.MirrorCS", {"start": v(15, -120) * mm, "end": v(15, -108) * mm});
            skArc(sketch, "E94.MirrorCS", {"start": v(15, -120) * mm, "mid": v(0, -135) * mm, "end": v(-15, -120) * mm});
            skCircle(sketch, "E95.0", {"center": v(60, -67.5) * mm, "radius": 4 * mm});
            skCircle(sketch, "E95.1", {"center": v(60, 67.5) * mm, "radius": 4 * mm});
            skCircle(sketch, "E95.2", {"center": v(-60, 67.5) * mm, "radius": 4 * mm});
            skCircle(sketch, "E95.3", {"center": v(-60, -67.5) * mm, "radius": 4 * mm});
            skSolve(sketch);
        }
        {
            var Q0;
            Q0 = qSketchRegion(id + "F16", true);
            var Q1;
            Q1=makeQuery(id+"F2.opExtrude","CAP_FACE",FACE,{"disambiguationData":[OSD([sQuery(id+"F0.wireOp",EDGE,"E12"),sQuery(id+"F0.wireOp",EDGE,"E13"),sQuery(id+"F0.wireOp",EDGE,"E14"),sQuery(id+"F0.wireOp",EDGE,"E15"),sQuery(id+"F0.wireOp",EDGE,"E17.filletArc"),sQuery(id+"F0.wireOp",EDGE,"E18.filletArc"),sQuery(id+"F0.wireOp",EDGE,"E19.filletArc"),sQuery(id+"F0.wireOp",EDGE,"E20.filletArc"),sQuery(id+"F0.wireOp",EDGE,"E25.0"),sQuery(id+"F0.wireOp",EDGE,"E25.1"),sQuery(id+"F0.wireOp",EDGE,"E25.2"),sQuery(id+"F0.wireOp",EDGE,"E25.3"),sQuery(id+"F0.wireOp",EDGE,"E25.4"),sQuery(id+"F0.wireOp",EDGE,"E25.5"),sQuery(id+"F0.wireOp",EDGE,"E25.6"),sQuery(id+"F0.wireOp",EDGE,"E25.7")])],"isStart":false});
            extrude(context, id + "F17", {"entities" : qUnion([Q0]), "endBound" : BoundingType.UP_TO_SURFACE, "depth" : 25 * mm, "endBoundEntityFace" : qUnion([Q1]), "offsetDistance" : 25 * mm});
        }
    });
